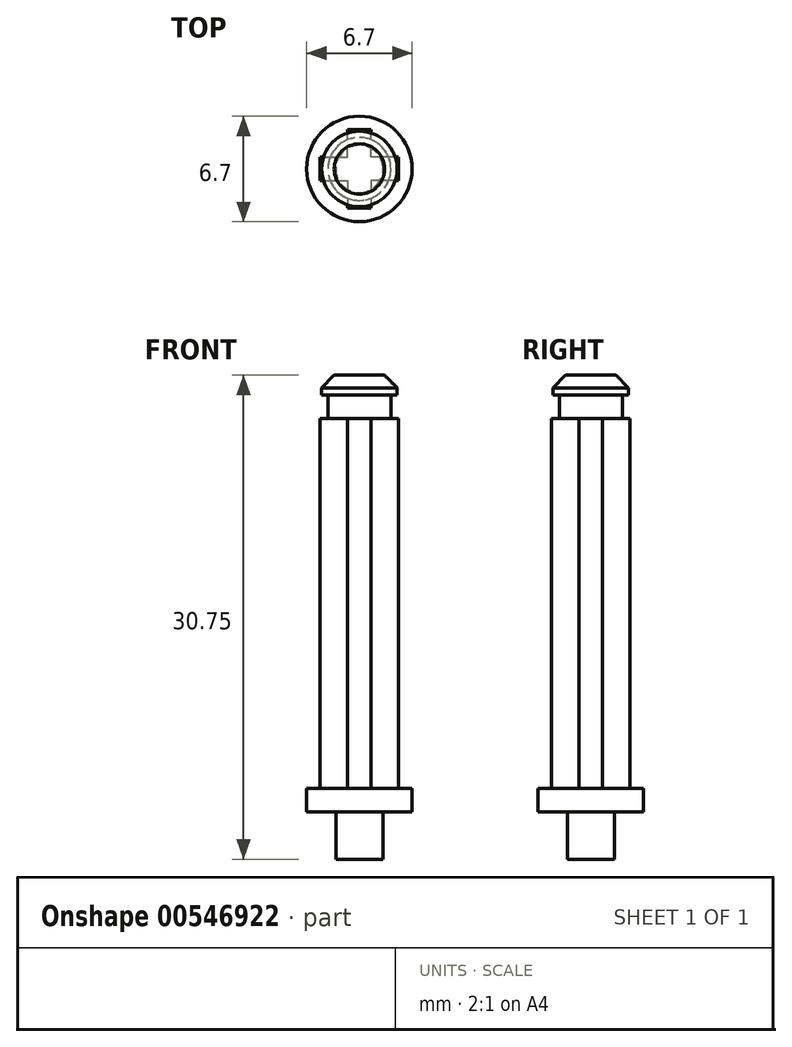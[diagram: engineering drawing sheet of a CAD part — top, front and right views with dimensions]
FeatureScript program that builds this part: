
annotation { "Feature Type Name" : "Feature", "Feature Type Description" : "" }
export const myFeature = defineFeature(function(context is Context, id is Id, definition is map)
    precondition{}
    {
        {
            var Q0;
            Q0=qCreatedBy(makeId("Top.planeOp"),FACE);
            var sketch = newSketch(context, id + "F0", { "sketchPlane" : qUnion([Q0])});
            skCircle(sketch, "E0", {"center": v(0, 0) * mm, "radius": 2 * mm});
            skSolve(sketch);
        }
        {
            var Q0;
            Q0=makeQuery(id+"F0.imprint","IMPRINT",FACE,{"disambiguationData":[TD([[makeQuery(id+"F0.imprint","IMPRINT",EDGE,{"derivedFrom":sQuery(id+"F0.wireOp",EDGE,"E0")}),1.0]])]});
            extrude(context, id + "F1", {"entities" : qUnion([Q0]), "depth" : 1.5 * mm, "offsetDistance" : 25 * mm});
        }
        {
            var Q0;
            Q0=makeQuery(id+"F1.opExtrude","CAP_FACE",FACE,{"disambiguationData":[OSD([sQuery(id+"F0.wireOp",EDGE,"E0")])],"isStart":false});
            var sketch = newSketch(context, id + "F2", { "sketchPlane" : qUnion([Q0])});
            skCircle(sketch, "E1", {"center": v(0, 0) * mm, "radius": 2.4 * mm});
            skSolve(sketch);
        }
        {
            var Q0;
            Q0=makeQuery(id+"F2.imprint","IMPRINT",FACE,{"disambiguationData":[TD([[makeQuery(id+"F2.imprint","IMPRINT",EDGE,{"derivedFrom":sQuery(id+"F2.wireOp",EDGE,"E1")}),1.0]])]});
            var Q1;
            Q1=makeQuery(id+"F2.imprint","IMPRINT",FACE,{"disambiguationData":[TD([[makeQuery(id+"F2.imprint","IMPRINT",EDGE,{"derivedFrom":makeQuery(id+"F1.opExtrude","CAP_EDGE",EDGE,{"disambiguationData":[OSD([sQuery(id+"F0.wireOp",EDGE,"E0")])],"isStart":false})}),1.0]])]});
            extrude(context, id + "F3", {"entities" : qUnion([Q0, Q1]), "operationType" : NewBodyOperationType.ADD, "depth" : 1.25 * mm, "offsetDistance" : 25 * mm});
        }
        {
            var Q0;
            Q0=makeQuery(id+"F3.opExtrude","CAP_EDGE",EDGE,{"disambiguationData":[OSD([sQuery(id+"F2.wireOp",EDGE,"E1")])],"isStart":false});
            chamfer(context, id + "F4", {"entities" : qUnion([Q0]), "width" : 0.8 * mm, "tangentPropagation" : true});
        }
        {
            var Q0;
            Q0=makeQuery(id+"F1.opExtrude","CAP_FACE",FACE,{"disambiguationData":[OSD([sQuery(id+"F0.wireOp",EDGE,"E0")])],"isStart":true});
            var sketch = newSketch(context, id + "F5", { "sketchPlane" : qUnion([Q0])});
            skLineSegment(sketch, "E2", {"start": v(-2.5, 0) * mm, "end": v(-2.5, -0.75) * mm});
            skLineSegment(sketch, "E3", {"start": v(-2.5, -0.75) * mm, "end": v(-0.75, -0.75) * mm});
            skLineSegment(sketch, "E4", {"start": v(-0.75, -0.75) * mm, "end": v(-0.75, -2.5) * mm});
            skLineSegment(sketch, "E5", {"start": v(-0.75, -2.5) * mm, "end": v(0, -2.5) * mm});
            skLineSegment(sketch, "E6.MirrorCS", {"start": v(-2.5, 0) * mm, "end": v(-2.5, 0.75) * mm});
            skLineSegment(sketch, "E7.MirrorCS", {"start": v(-2.5, 0.75) * mm, "end": v(-0.75, 0.75) * mm});
            skLineSegment(sketch, "E8.MirrorCS", {"start": v(-0.75, 2.5) * mm, "end": v(0, 2.5) * mm});
            skLineSegment(sketch, "E9.MirrorCS", {"start": v(-0.75, 0.75) * mm, "end": v(-0.75, 2.5) * mm});
            skLineSegment(sketch, "E10.MirrorCS", {"start": v(2.5, 0) * mm, "end": v(2.5, -0.75) * mm});
            skLineSegment(sketch, "E11.MirrorCS", {"start": v(2.5, -0.75) * mm, "end": v(0.75, -0.75) * mm});
            skLineSegment(sketch, "E12.MirrorCS", {"start": v(0.75, -0.75) * mm, "end": v(0.75, -2.5) * mm});
            skLineSegment(sketch, "E13.MirrorCS", {"start": v(0.75, -2.5) * mm, "end": v(0, -2.5) * mm});
            skLineSegment(sketch, "E14.MirrorCS", {"start": v(2.5, 0) * mm, "end": v(2.5, 0.75) * mm});
            skLineSegment(sketch, "E15.MirrorCS", {"start": v(2.5, 0.75) * mm, "end": v(0.75, 0.75) * mm});
            skLineSegment(sketch, "E16.MirrorCS", {"start": v(0.75, 2.5) * mm, "end": v(0, 2.5) * mm});
            skLineSegment(sketch, "E17.MirrorCS", {"start": v(0.75, 0.75) * mm, "end": v(0.75, 2.5) * mm});
            skSolve(sketch);
        }
        {
            var Q0;
            {var subQ4=sQuery(id+"F5.wireOp",EDGE,"E5");Q0=makeQuery(id+"F5.imprint","IMPRINT",FACE,{"disambiguationData":[TD([[makeQuery(id+"F5.imprint","IMPRINT",EDGE,{"derivedFrom":subQ4}),1.0]])]});}
            var Q1;
            {var subQ1=sQuery(id+"F5.wireOp",EDGE,"E6.MirrorCS");Q1=makeQuery(id+"F5.imprint","IMPRINT",FACE,{"disambiguationData":[TD([[makeQuery(id+"F5.imprint","IMPRINT",EDGE,{"derivedFrom":subQ1}),-1.0]])]});}
            var Q2;
            {var subQ4=sQuery(id+"F5.wireOp",EDGE,"E8.MirrorCS");Q2=makeQuery(id+"F5.imprint","IMPRINT",FACE,{"disambiguationData":[TD([[makeQuery(id+"F5.imprint","IMPRINT",EDGE,{"derivedFrom":subQ4}),-1.0]])]});}
            var Q3;
            {var subQ5=sQuery(id+"F5.wireOp",EDGE,"E10.MirrorCS");Q3=makeQuery(id+"F5.imprint","IMPRINT",FACE,{"disambiguationData":[TD([[makeQuery(id+"F5.imprint","IMPRINT",EDGE,{"derivedFrom":subQ5}),-1.0]])]});}
            var Q4;
            {var subQ3=sQuery(id+"F5.wireOp",EDGE,"E3");var subQ12=sQuery(id+"F5.wireOp",EDGE,"E4");var subQ13=makeQuery(id+"F5.imprint","INTERSECT",VERTEX,{"derivedFrom":[subQ12,subQ3]});Q4=makeQuery(id+"F5.imprint","IMPRINT",FACE,{"disambiguationData":[TD([[makeQuery(id+"F5.imprint","IMPRINT",EDGE,{"disambiguationData":[TD([[subQ13,-1.0]])],"derivedFrom":subQ12}),1.0]])]});}
            extrude(context, id + "F6", {"entities" : qUnion([Q0, Q1, Q2, Q3, Q4]), "operationType" : NewBodyOperationType.ADD, "depth" : 23.5 * mm, "offsetDistance" : 25 * mm});
        }
        {
            var Q0;
            Q0=makeQuery(id+"F6.opExtrude","CAP_FACE",FACE,{"disambiguationData":[OSD([sQuery(id+"F5.wireOp",EDGE,"E6.MirrorCS"),sQuery(id+"F5.wireOp",EDGE,"E4"),sQuery(id+"F5.wireOp",EDGE,"E2"),sQuery(id+"F5.wireOp",EDGE,"E7.MirrorCS"),sQuery(id+"F5.wireOp",EDGE,"E9.MirrorCS"),sQuery(id+"F5.wireOp",EDGE,"E3"),sQuery(id+"F5.wireOp",EDGE,"E5"),sQuery(id+"F5.wireOp",EDGE,"E8.MirrorCS"),sQuery(id+"F5.wireOp",EDGE,"E10.MirrorCS"),sQuery(id+"F5.wireOp",EDGE,"E16.MirrorCS"),sQuery(id+"F5.wireOp",EDGE,"E13.MirrorCS"),sQuery(id+"F5.wireOp",EDGE,"E11.MirrorCS"),sQuery(id+"F5.wireOp",EDGE,"E17.MirrorCS"),sQuery(id+"F5.wireOp",EDGE,"E15.MirrorCS"),sQuery(id+"F5.wireOp",EDGE,"E14.MirrorCS"),sQuery(id+"F5.wireOp",EDGE,"E12.MirrorCS")])],"isStart":false});
            var sketch = newSketch(context, id + "F7", { "sketchPlane" : qUnion([Q0])});
            skCircle(sketch, "E18", {"center": v(0, 0) * mm, "radius": 3.35 * mm});
            skSolve(sketch);
        }
        {
            var Q0;
            Q0=makeQuery(id+"F7.imprint","IMPRINT",FACE,{"disambiguationData":[TD([[makeQuery(id+"F7.imprint","IMPRINT",EDGE,{"derivedFrom":sQuery(id+"F7.wireOp",EDGE,"E18")}),1.0]])]});
            var Q1;
            Q1=makeQuery(id+"F7.imprint","IMPRINT",FACE,{"disambiguationData":[TD([[makeQuery(id+"F7.imprint","IMPRINT",EDGE,{"derivedFrom":makeQuery(id+"F6.opExtrude","CAP_EDGE",EDGE,{"disambiguationData":[OSD([sQuery(id+"F5.wireOp",EDGE,"E4")])],"isStart":false})}),1.0]])]});
            extrude(context, id + "F8", {"entities" : qUnion([Q0, Q1]), "operationType" : NewBodyOperationType.ADD, "depth" : 1.5 * mm, "offsetDistance" : 25 * mm});
        }
        {
            var Q0;
            Q0=makeQuery(id+"F8.opExtrude","CAP_FACE",FACE,{"disambiguationData":[OSD([sQuery(id+"F7.wireOp",EDGE,"E18")])],"isStart":false});
            var sketch = newSketch(context, id + "F9", { "sketchPlane" : qUnion([Q0])});
            skCircle(sketch, "E19", {"center": v(0, 0) * mm, "radius": 1.5 * mm});
            skSolve(sketch);
        }
        {
            var Q0;
            Q0=makeQuery(id+"F9.imprint","IMPRINT",FACE,{"disambiguationData":[TD([[makeQuery(id+"F9.imprint","IMPRINT",EDGE,{"derivedFrom":sQuery(id+"F9.wireOp",EDGE,"E19")}),1.0]])]});
            extrude(context, id + "F10", {"entities" : qUnion([Q0]), "operationType" : NewBodyOperationType.ADD, "depth" : 3 * mm, "offsetDistance" : 25 * mm});
        }
    });
